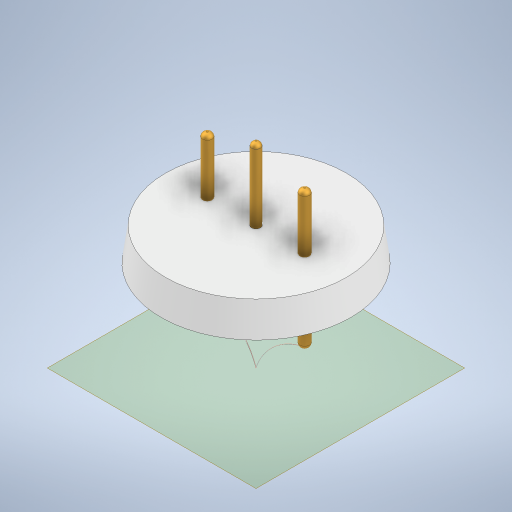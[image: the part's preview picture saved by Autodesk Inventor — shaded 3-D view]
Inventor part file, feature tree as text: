
AUTODESK INVENTOR PART (.ipt)
format: ipt  version: 2023 (Build 270158000, 158)  size: 333,824 bytes
history: native  units: mm
features: sketch x5, other x2, extrude x2, revolve x1, fillet x1, sweep x1, plane x1
ambient origin geometry x8: Origin, YZ Plane, XZ Plane, XY Plane, X Axis, Y Axis, Z Axis, Center Point
bodies: Solid1 (feature_tree)
feature tree (13):
  other  "Filament"
  revolve  "Revolution1"  [1 undecoded]
  extrude  "Extrusion1"  TaperAngle=90.0deg  [1 undecoded]
  extrude  "Extrusion2"  Depth=1.2mm
  fillet  "Fillet1"  Radius=6.0mm
  sweep  "Sweep1"
  plane  "Work Plane1"
  sketch  "Sketch1"  dims[d0=23.4mm d1=22.3mm]
  sketch  "Sketch2"  dims[d2=4.0mm d3=90.0deg]
  sketch  "Sketch3"  dims[d4=1.2mm d5=1.2mm d6=6.0mm]
  sketch  "Sketch4"  dims[d7=6.0mm d8=6.0mm d9=11.0mm d10=0.0mm d11=0.0mm]
  sketch  "Sketch5"  dims[d12=1.1mm d13=9.0mm d14=0.0mm d15=0.5mm d16=11.2mm d17=8.0mm d18=0.1mm d19=0.0mm d20=0.0mm]
  other  "Pins"
note: 2 required parameter values undecoded (feature->parameter linkage not recoverable at this tier; creation-order binding heuristic only, values carry confidence <= 0.55)